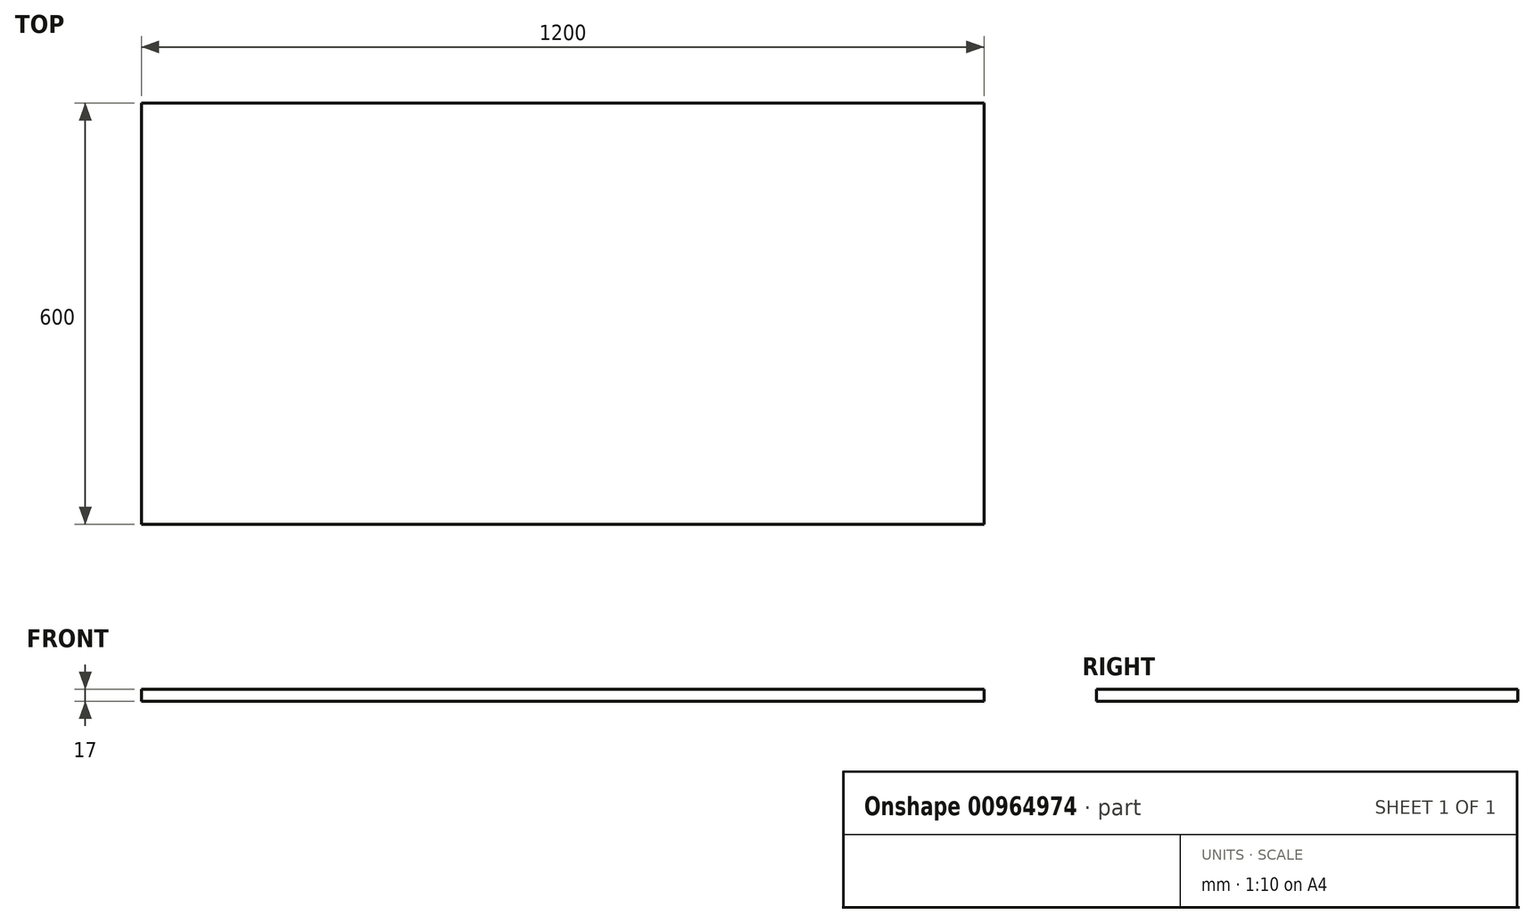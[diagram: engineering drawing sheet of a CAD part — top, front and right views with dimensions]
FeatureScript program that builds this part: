
annotation { "Feature Type Name" : "Feature", "Feature Type Description" : "" }
export const myFeature = defineFeature(function(context is Context, id is Id, definition is map)
    precondition{}
    {
        {
            var Q0;
            Q0=qCreatedBy(makeId("Top.planeOp"),FACE);
            var sketch = newSketch(context, id + "F0", { "sketchPlane" : qUnion([Q0])});
            skLineSegment(sketch, "E0.bottom", {"start": v(-600, 300) * mm, "end": v(600, 300) * mm});
            skLineSegment(sketch, "E0.top", {"start": v(-600, -300) * mm, "end": v(600, -300) * mm});
            skLineSegment(sketch, "E0.left", {"start": v(-600, 300) * mm, "end": v(-600, -300) * mm});
            skLineSegment(sketch, "E0.right", {"start": v(600, 300) * mm, "end": v(600, -300) * mm});
            skPoint(sketch, "E0.middle", {"position": v(0, 0) * mm});
            skSolve(sketch);
        }
        {
            var Q0;
            Q0=makeQuery(id+"F0.imprint","IMPRINT",FACE,{"disambiguationData":[TD([[makeQuery(id+"F0.imprint","IMPRINT",EDGE,{"derivedFrom":sQuery(id+"F0.wireOp",EDGE,"E0.bottom")}),-1.0]])]});
            extrude(context, id + "F1", {"entities" : qUnion([Q0]), "depth" : 17 * mm, "offsetDistance" : 25 * mm});
        }
    });
